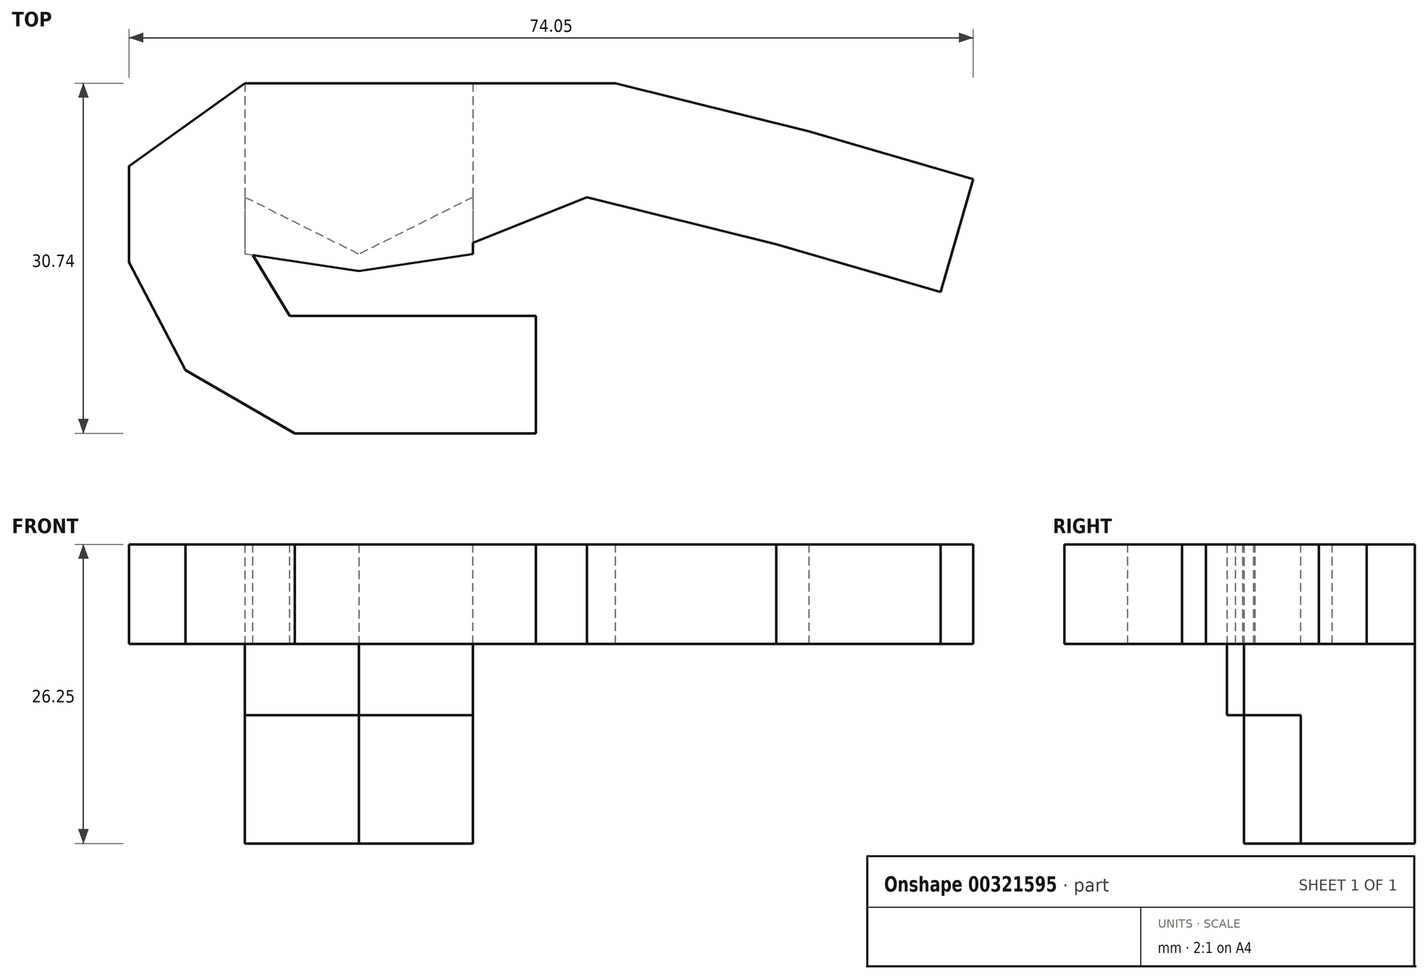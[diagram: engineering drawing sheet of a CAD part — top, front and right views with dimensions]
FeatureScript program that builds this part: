
annotation { "Feature Type Name" : "Feature", "Feature Type Description" : "" }
export const myFeature = defineFeature(function(context is Context, id is Id, definition is map)
    precondition{}
    {
        {
            var Q0;
            Q0=qCreatedBy(makeId("Top.planeOp"),FACE);
            var sketch = newSketch(context, id + "F0", { "sketchPlane" : qUnion([Q0])});
            skLineSegment(sketch, "E0", {"start": v(-103.7, 30.74) * mm, "end": v(-83.7, 30.74) * mm});
            skLineSegment(sketch, "E1", {"start": v(-103.7, 30.74) * mm, "end": v(-103.7, 20.74) * mm});
            skLineSegment(sketch, "E2", {"start": v(-83.7, 30.74) * mm, "end": v(-83.7, 20.74) * mm});
            skLineSegment(sketch, "E3", {"start": v(-103.7, 30.74) * mm, "end": v(-93.7, 30.74) * mm});
            skLineSegment(sketch, "E4", {"start": v(-93.7, 30.74) * mm, "end": v(-93.7, 15.74) * mm});
            skLineSegment(sketch, "E5", {"start": v(-103.7, 20.74) * mm, "end": v(-93.7, 15.74) * mm});
            skLineSegment(sketch, "E6", {"start": v(-83.7, 20.74) * mm, "end": v(-93.7, 15.74) * mm});
            skSolve(sketch);
        }
        {
            var Q0;
            Q0=makeQuery(id+"F0.imprint","IMPRINT",FACE,{"disambiguationData":[TD([[makeQuery(id+"F0.imprint","IMPRINT",EDGE,{"derivedFrom":sQuery(id+"F0.wireOp",EDGE,"E0")}),-1.0]])]});
            var Q1;
            Q1=makeQuery(id+"F0.imprint","IMPRINT",FACE,{"disambiguationData":[TD([[makeQuery(id+"F0.imprint","IMPRINT",EDGE,{"derivedFrom":sQuery(id+"F0.wireOp",EDGE,"E1")}),1.0]])]});
            extrude(context, id + "F1", {"entities" : qUnion([Q0, Q1]), "depth" : 11.25 * mm});
        }
        {
            var Q0;
            Q0=makeQuery(id+"F1.opExtrude","CAP_FACE",FACE,{"disambiguationData":[OSD([sQuery(id+"F0.wireOp",EDGE,"E0"),sQuery(id+"F0.wireOp",EDGE,"E1"),sQuery(id+"F0.wireOp",EDGE,"E2"),sQuery(id+"F0.wireOp",EDGE,"E3"),sQuery(id+"F0.wireOp",EDGE,"x63AXPWN-MAJO-YShk-7xWk-JNa9fSzDsO9F"),sQuery(id+"F0.wireOp",EDGE,"O9R0ehpi-I5dL-M14p-Romt-SMtRQ81g7BhE")])],"isStart":false});
            var sketch = newSketch(context, id + "F2", { "sketchPlane" : qUnion([Q0])});
            skLineSegment(sketch, "E7.bottom", {"start": v(-103.7, 30.74) * mm, "end": v(-83.7, 30.74) * mm});
            skLineSegment(sketch, "E7.left", {"start": v(-103.7, 30.74) * mm, "end": v(-103.7, 15.74) * mm});
            skLineSegment(sketch, "E7.right", {"start": v(-83.7, 30.74) * mm, "end": v(-83.7, 15.74) * mm});
            skLineSegment(sketch, "E8", {"start": v(-93.7, 30.74) * mm, "end": v(-93.7, 14.24) * mm});
            skLineSegment(sketch, "E9", {"start": v(-93.7, 14.24) * mm, "end": v(-103.7, 15.74) * mm});
            skLineSegment(sketch, "E10", {"start": v(-93.7, 14.24) * mm, "end": v(-83.7, 15.74) * mm});
            skSolve(sketch);
        }
        {
            var Q0;
            {var subQ2=sQuery(id+"F2.wireOp",EDGE,"E9");Q0=makeQuery(id+"F2.imprint","IMPRINT",FACE,{"disambiguationData":[TD([[makeQuery(id+"F2.imprint","IMPRINT",EDGE,{"derivedFrom":subQ2}),-1.0]])]});}
            var Q1;
            {var subQ5=makeQuery(id+"F1.opExtrude","CAP_EDGE",EDGE,{"disambiguationData":[OSD([sQuery(id+"F0.wireOp",EDGE,"E5")])],"isStart":false});Q1=makeQuery(id+"F2.imprint","IMPRINT",FACE,{"disambiguationData":[TD([[makeQuery(id+"F2.imprint","IMPRINT",EDGE,{"derivedFrom":subQ5}),1.0]])]});}
            var Q2;
            {var subQ2=sQuery(id+"F2.wireOp",EDGE,"E10");Q2=makeQuery(id+"F2.imprint","IMPRINT",FACE,{"disambiguationData":[TD([[makeQuery(id+"F2.imprint","IMPRINT",EDGE,{"derivedFrom":subQ2}),1.0]])]});}
            var Q3;
            {var subQ5=makeQuery(id+"F1.opExtrude","CAP_EDGE",EDGE,{"disambiguationData":[OSD([sQuery(id+"F0.wireOp",EDGE,"E6")])],"isStart":false});Q3=makeQuery(id+"F2.imprint","IMPRINT",FACE,{"disambiguationData":[TD([[makeQuery(id+"F2.imprint","IMPRINT",EDGE,{"derivedFrom":subQ5}),-1.0]])]});}
            extrude(context, id + "F3", {"entities" : qUnion([Q0, Q1, Q2, Q3]), "operationType" : NewBodyOperationType.ADD, "depth" : 15 * mm});
        }
        {
            var Q0;
            Q0=makeQuery(id+"F3.opExtrude","CAP_FACE",FACE,{"disambiguationData":[OSD([sQuery(id+"F2.wireOp",EDGE,"E7.bottom"),sQuery(id+"F2.wireOp",EDGE,"E7.left"),sQuery(id+"F2.wireOp",EDGE,"E7.right"),sQuery(id+"F2.wireOp",EDGE,"E9"),sQuery(id+"F2.wireOp",EDGE,"E10")])],"isStart":false});
            var sketch = newSketch(context, id + "F4", { "sketchPlane" : qUnion([Q0])});
            skLineSegment(sketch, "E11.bottom", {"start": v(-83.7, 30.74) * mm, "end": v(-71.2, 30.74) * mm});
            skLineSegment(sketch, "E12.bottom", {"start": v(-103.7, 30.74) * mm, "end": v(-113.7, 30.74) * mm});
            skLineSegment(sketch, "E12.top", {"start": v(-103.7, 20.74) * mm, "end": v(-113.7, 20.74) * mm});
            skLineSegment(sketch, "E12.left", {"start": v(-103.7, 30.74) * mm, "end": v(-103.7, 20.74) * mm});
            skLineSegment(sketch, "E12.right", {"start": v(-113.7, 30.74) * mm, "end": v(-113.7, 20.74) * mm});
            skLineSegment(sketch, "E13", {"start": v(-83.7, 30.74) * mm, "end": v(-83.7, 16.74) * mm});
            skLineSegment(sketch, "E14", {"start": v(-83.7, 16.74) * mm, "end": v(-73.7, 20.74) * mm});
            skLineSegment(sketch, "E15", {"start": v(-73.7, 20.74) * mm, "end": v(-71.2, 30.74) * mm});
            skSolve(sketch);
        }
        {
            var Q0;
            Q0=makeQuery(id+"F4.imprint","IMPRINT",FACE,{"disambiguationData":[TD([[makeQuery(id+"F4.imprint","IMPRINT",EDGE,{"derivedFrom":sQuery(id+"F4.wireOp",EDGE,"E11.bottom")}),-1.0]])]});
            extrude(context, id + "F5", {"entities" : qUnion([Q0]), "operationType" : NewBodyOperationType.ADD, "oppositeDirection" : true, "depth" : 8.75 * mm});
        }
        {
            var Q0;
            Q0=makeQuery(id+"F5.boolean.opBoolean","MERGE",FACE,{"derivedFrom":[makeQuery(id+"F3.opExtrude","CAP_FACE",FACE,{"disambiguationData":[OSD([sQuery(id+"F2.wireOp",EDGE,"E7.bottom"),sQuery(id+"F2.wireOp",EDGE,"E7.left"),sQuery(id+"F2.wireOp",EDGE,"E7.right"),sQuery(id+"F2.wireOp",EDGE,"E9"),sQuery(id+"F2.wireOp",EDGE,"E10")])],"isStart":false}),makeQuery(id+"F5.opExtrude","CAP_FACE",FACE,{"disambiguationData":[OSD([sQuery(id+"F4.wireOp",EDGE,"E11.bottom"),sQuery(id+"F4.wireOp",EDGE,"E11.right"),sQuery(id+"F4.wireOp",EDGE,"E13"),sQuery(id+"F4.wireOp",EDGE,"E14")])],"isStart":true})]});
            var sketch = newSketch(context, id + "F6", { "sketchPlane" : qUnion([Q0])});
            skLineSegment(sketch, "E16", {"start": v(-103.7, 30.74) * mm, "end": v(-103.7, 16.74) * mm});
            skLineSegment(sketch, "E17", {"start": v(-103.7, 30.74) * mm, "end": v(-113.87, 23.47) * mm});
            skLineSegment(sketch, "E18", {"start": v(-113.87, 23.47) * mm, "end": v(-113.87, 15) * mm});
            skLineSegment(sketch, "E19", {"start": v(-113.87, 15) * mm, "end": v(-103.7, 16.74) * mm});
            skSolve(sketch);
        }
        {
            var Q0;
            Q0=makeQuery(id+"F6.imprint","IMPRINT",FACE,{"disambiguationData":[TD([[makeQuery(id+"F6.imprint","IMPRINT",EDGE,{"derivedFrom":sQuery(id+"F6.wireOp",EDGE,"E16")}),-1.0]])]});
            extrude(context, id + "F7", {"entities" : qUnion([Q0]), "oppositeDirection" : true, "depth" : 8.75 * mm});
        }
        {
            var Q0;
            Q0=makeQuery(id+"F5.boolean.opBoolean","MERGE",FACE,{"derivedFrom":[makeQuery(id+"F3.opExtrude","CAP_FACE",FACE,{"disambiguationData":[OSD([sQuery(id+"F2.wireOp",EDGE,"E7.bottom"),sQuery(id+"F2.wireOp",EDGE,"E7.left"),sQuery(id+"F2.wireOp",EDGE,"E7.right"),sQuery(id+"F2.wireOp",EDGE,"E9"),sQuery(id+"F2.wireOp",EDGE,"E10")])],"isStart":false}),makeQuery(id+"F5.opExtrude","CAP_FACE",FACE,{"disambiguationData":[OSD([sQuery(id+"F4.wireOp",EDGE,"E11.bottom"),sQuery(id+"F4.wireOp",EDGE,"E13"),sQuery(id+"F4.wireOp",EDGE,"E14"),sQuery(id+"F4.wireOp",EDGE,"E15")])],"isStart":true})]});
            var sketch = newSketch(context, id + "F8", { "sketchPlane" : qUnion([Q0])});
            skLineSegment(sketch, "E20", {"start": v(-73.7, 20.74) * mm, "end": v(-71.2, 30.74) * mm});
            skLineSegment(sketch, "E21", {"start": v(-71.2, 30.74) * mm, "end": v(-54.22, 26.5) * mm});
            skLineSegment(sketch, "E22", {"start": v(-73.7, 20.74) * mm, "end": v(-57.1, 16.59) * mm});
            skLineSegment(sketch, "E23", {"start": v(-57.1, 16.59) * mm, "end": v(-54.22, 26.5) * mm});
            skSolve(sketch);
        }
        {
            var Q0;
            Q0=makeQuery(id+"F8.imprint","IMPRINT",FACE,{"disambiguationData":[TD([[makeQuery(id+"F8.imprint","IMPRINT",EDGE,{"derivedFrom":sQuery(id+"F8.wireOp",EDGE,"E20")}),-1.0]])]});
            extrude(context, id + "F9", {"entities" : qUnion([Q0]), "operationType" : NewBodyOperationType.ADD, "oppositeDirection" : true, "depth" : 8.75 * mm});
        }
        {
            var Q0;
            Q0=makeQuery(id+"F7.opExtrude","CAP_FACE",FACE,{"disambiguationData":[OSD([sQuery(id+"F6.wireOp",EDGE,"E16"),sQuery(id+"F6.wireOp",EDGE,"E17"),sQuery(id+"F6.wireOp",EDGE,"E18"),sQuery(id+"F6.wireOp",EDGE,"E19")])],"isStart":true});
            var sketch = newSketch(context, id + "F10", { "sketchPlane" : qUnion([Q0])});
            skLineSegment(sketch, "E24", {"start": v(-113.87, 15) * mm, "end": v(-108.92, 5.54) * mm});
            skLineSegment(sketch, "E25", {"start": v(-99.78, 10.32) * mm, "end": v(-103.7, 16.74) * mm});
            skLineSegment(sketch, "E26", {"start": v(-99.78, 10.32) * mm, "end": v(-78.2, 10.32) * mm});
            skLineSegment(sketch, "E27", {"start": v(-78.2, 10.32) * mm, "end": v(-78.2, 0) * mm});
            skLineSegment(sketch, "E28", {"start": v(-78.2, 0) * mm, "end": v(-99.32, 0) * mm});
            skLineSegment(sketch, "E29", {"start": v(-108.92, 5.54) * mm, "end": v(-99.32, 0) * mm});
            skSolve(sketch);
        }
        {
            var Q0;
            Q0=makeQuery(id+"F10.imprint","IMPRINT",FACE,{"disambiguationData":[TD([[makeQuery(id+"F10.imprint","IMPRINT",EDGE,{"derivedFrom":sQuery(id+"F10.wireOp",EDGE,"E24")}),1.0]])]});
            extrude(context, id + "F11", {"entities" : qUnion([Q0]), "operationType" : NewBodyOperationType.ADD, "oppositeDirection" : true, "depth" : 8.75 * mm});
        }
        {
            var Q0;
            Q0=makeQuery(id+"F11.boolean.opBoolean","MERGE",FACE,{"derivedFrom":[makeQuery(id+"F9.boolean.opBoolean","MERGE",FACE,{"derivedFrom":[makeQuery(id+"F5.boolean.opBoolean","MERGE",FACE,{"derivedFrom":[makeQuery(id+"F3.opExtrude","CAP_FACE",FACE,{"disambiguationData":[OSD([sQuery(id+"F2.wireOp",EDGE,"E7.bottom"),sQuery(id+"F2.wireOp",EDGE,"E7.left"),sQuery(id+"F2.wireOp",EDGE,"E7.right"),sQuery(id+"F2.wireOp",EDGE,"E9"),sQuery(id+"F2.wireOp",EDGE,"E10")])],"isStart":false}),makeQuery(id+"F5.opExtrude","CAP_FACE",FACE,{"disambiguationData":[OSD([sQuery(id+"F4.wireOp",EDGE,"E11.bottom"),sQuery(id+"F4.wireOp",EDGE,"E13"),sQuery(id+"F4.wireOp",EDGE,"E14"),sQuery(id+"F4.wireOp",EDGE,"E15")])],"isStart":true})]}),makeQuery(id+"F9.opExtrude","CAP_FACE",FACE,{"disambiguationData":[OSD([sQuery(id+"F8.wireOp",EDGE,"E20"),sQuery(id+"F8.wireOp",EDGE,"E21"),sQuery(id+"F8.wireOp",EDGE,"E22"),sQuery(id+"F8.wireOp",EDGE,"E23")])],"isStart":true})]}),makeQuery(id+"F11.opExtrude","CAP_FACE",FACE,{"disambiguationData":[OSD([sQuery(id+"F6.wireOp",EDGE,"E19"),sQuery(id+"F10.wireOp",EDGE,"E24"),sQuery(id+"F10.wireOp",EDGE,"E25"),sQuery(id+"F10.wireOp",EDGE,"E26"),sQuery(id+"F10.wireOp",EDGE,"E27"),sQuery(id+"F10.wireOp",EDGE,"E28"),sQuery(id+"F10.wireOp",EDGE,"E29")])],"isStart":true})]});
            var sketch = newSketch(context, id + "F12", { "sketchPlane" : qUnion([Q0])});
            skLineSegment(sketch, "E30", {"start": v(-57.1, 16.59) * mm, "end": v(-42.7, 12.4) * mm});
            skLineSegment(sketch, "E31", {"start": v(-54.22, 26.5) * mm, "end": v(-39.82, 22.3) * mm});
            skLineSegment(sketch, "E32", {"start": v(-39.82, 22.3) * mm, "end": v(-42.7, 12.4) * mm});
            skSolve(sketch);
        }
        {
            var Q0;
            Q0=makeQuery(id+"F12.imprint","IMPRINT",FACE,{"disambiguationData":[TD([[makeQuery(id+"F12.imprint","IMPRINT",EDGE,{"derivedFrom":sQuery(id+"F12.wireOp",EDGE,"E30")}),1.0]])]});
            extrude(context, id + "F13", {"entities" : qUnion([Q0]), "operationType" : NewBodyOperationType.ADD, "oppositeDirection" : true, "depth" : 8.75 * mm});
        }
    });
